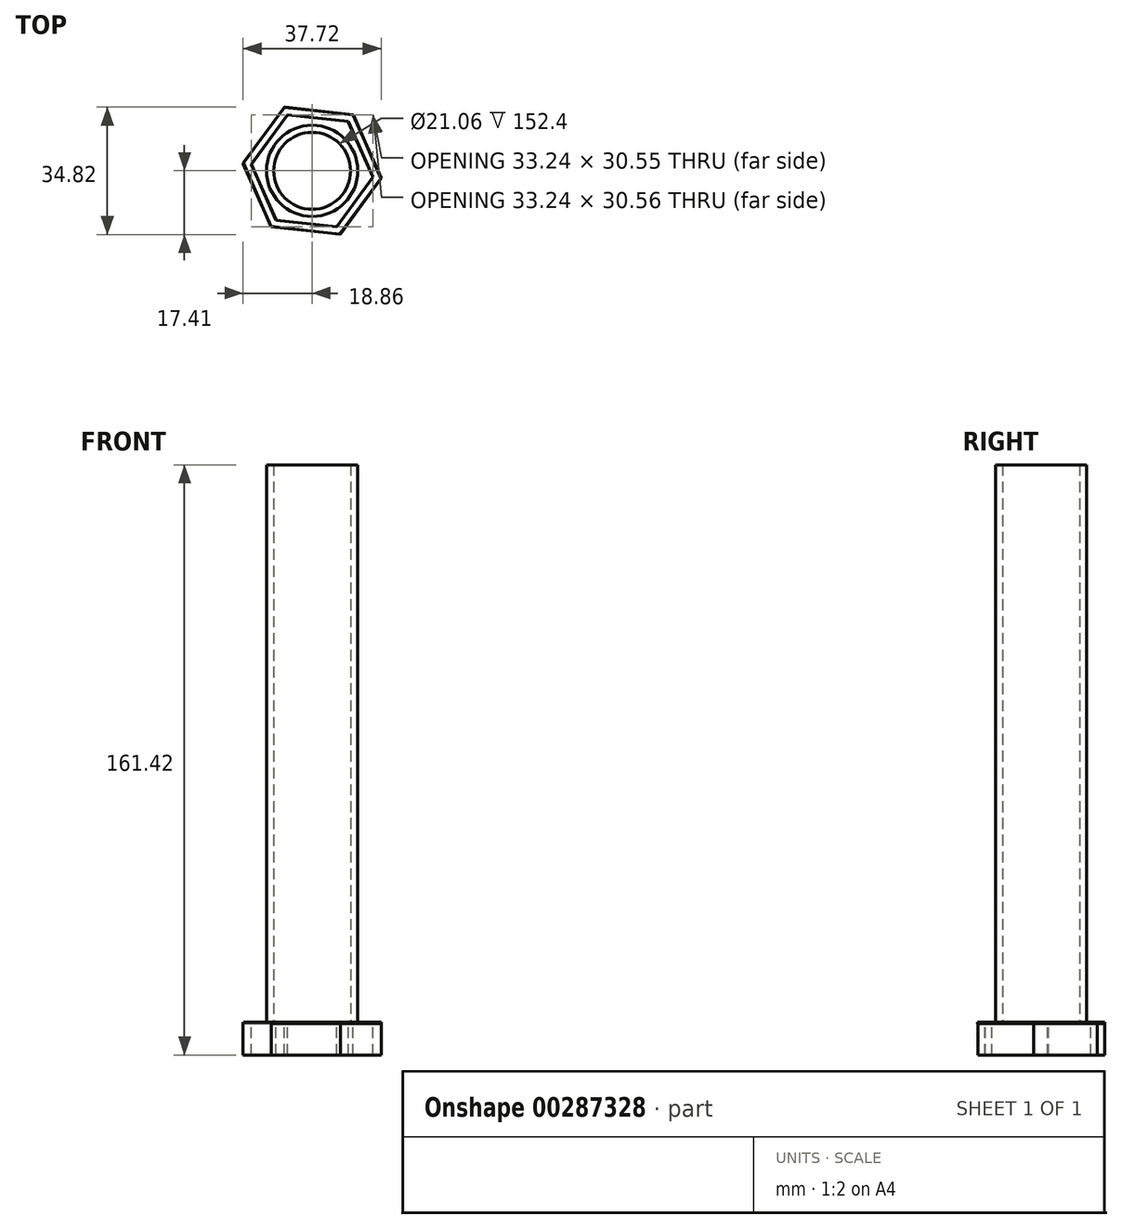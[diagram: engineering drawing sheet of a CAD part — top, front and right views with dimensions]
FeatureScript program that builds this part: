
annotation { "Feature Type Name" : "Feature", "Feature Type Description" : "" }
export const myFeature = defineFeature(function(context is Context, id is Id, definition is map)
    precondition{}
    {
        {
            var Q0;
            Q0=qCreatedBy(makeId("Top.planeOp"),FACE);
            var sketch = newSketch(context, id + "F0", { "sketchPlane" : qUnion([Q0])});
            skCircle(sketch, "E0.cCircle", {"center": v(0, 0) * mm, "radius": 14.47 * mm, "construction": true});
            skLineSegment(sketch, "E0.0", {"start": v(16.62, -1.78) * mm, "end": v(6.77, -15.28) * mm});
            skLineSegment(sketch, "E0.1", {"start": v(6.77, -15.28) * mm, "end": v(-9.85, -13.5) * mm});
            skLineSegment(sketch, "E0.2", {"start": v(-9.85, -13.5) * mm, "end": v(-16.62, 1.78) * mm});
            skLineSegment(sketch, "E0.3", {"start": v(-16.62, 1.78) * mm, "end": v(-6.77, 15.28) * mm});
            skLineSegment(sketch, "E0.4", {"start": v(-6.77, 15.28) * mm, "end": v(9.85, 13.5) * mm});
            skLineSegment(sketch, "E0.5", {"start": v(9.85, 13.5) * mm, "end": v(16.62, -1.78) * mm});
            skPoint(sketch, "E0.0.midPoint", {"position": v(11.7, -8.53) * mm});
            skCircle(sketch, "E1.cCircle", {"center": v(0, 0) * mm, "radius": 16.43 * mm, "construction": true});
            skLineSegment(sketch, "E1.0", {"start": v(18.86, -2.02) * mm, "end": v(7.69, -17.34) * mm});
            skLineSegment(sketch, "E1.1", {"start": v(7.69, -17.34) * mm, "end": v(-11.18, -15.33) * mm});
            skLineSegment(sketch, "E1.2", {"start": v(-11.18, -15.33) * mm, "end": v(-18.86, 2.02) * mm});
            skLineSegment(sketch, "E1.3", {"start": v(-18.86, 2.02) * mm, "end": v(-7.69, 17.34) * mm});
            skLineSegment(sketch, "E1.4", {"start": v(-7.69, 17.34) * mm, "end": v(11.18, 15.33) * mm});
            skLineSegment(sketch, "E1.5", {"start": v(11.18, 15.33) * mm, "end": v(18.86, -2.02) * mm});
            skPoint(sketch, "E1.0.midPoint", {"position": v(13.28, -9.68) * mm});
            skSolve(sketch);
        }
        {
            var Q0;
            Q0=makeQuery(id+"F0.imprint","IMPRINT",FACE,{"disambiguationData":[TD([[makeQuery(id+"F0.imprint","IMPRINT",EDGE,{"derivedFrom":sQuery(id+"F0.wireOp",EDGE,"E0.0")}),1.0]])]});
            extrude(context, id + "F1", {"entities" : qUnion([Q0]), "oppositeDirection" : true, "depth" : 9.02 * mm});
        }
        {
            var Q0;
            Q0=qCreatedBy(makeId("Top.planeOp"),FACE);
            var sketch = newSketch(context, id + "F2", { "sketchPlane" : qUnion([Q0])});
            skCircle(sketch, "E2", {"center": v(0, 0) * mm, "radius": 10.53 * mm});
            skCircle(sketch, "E3", {"center": v(0, 0) * mm, "radius": 12.48 * mm});
            skSolve(sketch);
        }
        {
            var Q0;
            Q0=makeQuery(id+"F2.imprint","IMPRINT",FACE,{"disambiguationData":[TD([[makeQuery(id+"F2.imprint","IMPRINT",EDGE,{"derivedFrom":sQuery(id+"F2.wireOp",EDGE,"E2")}),-1.0]])]});
            extrude(context, id + "F3", {"entities" : qUnion([Q0]), "depth" : 152.4 * mm});
        }
        {
            var Q0;
            Q0=makeQuery(id+"F0.imprint","IMPRINT",FACE,{"disambiguationData":[TD([[makeQuery(id+"F0.imprint","IMPRINT",EDGE,{"derivedFrom":sQuery(id+"F0.wireOp",EDGE,"E0.0")}),-1.0]])]});
            var sketch = newSketch(context, id + "F4", { "sketchPlane" : qUnion([Q0])});
            skCircle(sketch, "E4.cCircle", {"center": v(0, 0) * mm, "radius": 14.47 * mm, "construction": true});
            skLineSegment(sketch, "E4.0", {"start": v(16.6, -1.93) * mm, "end": v(6.63, -15.34) * mm});
            skLineSegment(sketch, "E4.1", {"start": v(6.63, -15.34) * mm, "end": v(-9.97, -13.41) * mm});
            skLineSegment(sketch, "E4.2", {"start": v(-9.97, -13.41) * mm, "end": v(-16.6, 1.93) * mm});
            skLineSegment(sketch, "E4.3", {"start": v(-16.6, 1.93) * mm, "end": v(-6.63, 15.34) * mm});
            skLineSegment(sketch, "E4.4", {"start": v(-6.63, 15.34) * mm, "end": v(9.97, 13.41) * mm});
            skLineSegment(sketch, "E4.5", {"start": v(9.97, 13.41) * mm, "end": v(16.6, -1.93) * mm});
            skPoint(sketch, "E4.0.midPoint", {"position": v(11.62, -8.63) * mm});
            skSolve(sketch);
        }
        {
            var Q0;
            Q0=qCreatedBy(makeId("Top.planeOp"),FACE);
            var sketch = newSketch(context, id + "F5", { "sketchPlane" : qUnion([Q0])});
            skCircle(sketch, "E5", {"center": v(0, 0) * mm, "radius": 10.53 * mm});
            skSolve(sketch);
        }
        {
            var Q0;
            Q0 = qSketchRegion(id + "F5", true);
            extrude(context, id + "F6", {"entities" : qUnion([Q0]), "operationType" : NewBodyOperationType.REMOVE, "depth" : 25.4 * mm});
        }
        {
            var Q0;
            Q0=qCreatedBy(makeId("Top.planeOp"),FACE);
            var sketch = newSketch(context, id + "F7", { "sketchPlane" : qUnion([Q0])});
            skCircle(sketch, "E6.cCircle", {"center": v(0, 0) * mm, "radius": 14.47 * mm, "construction": true});
            skLineSegment(sketch, "E6.0", {"start": v(16.62, -1.78) * mm, "end": v(6.77, -15.28) * mm});
            skLineSegment(sketch, "E6.1", {"start": v(6.77, -15.28) * mm, "end": v(-9.85, -13.5) * mm});
            skLineSegment(sketch, "E6.2", {"start": v(-9.85, -13.5) * mm, "end": v(-16.62, 1.78) * mm});
            skLineSegment(sketch, "E6.3", {"start": v(-16.62, 1.78) * mm, "end": v(-6.77, 15.28) * mm});
            skLineSegment(sketch, "E6.4", {"start": v(-6.77, 15.28) * mm, "end": v(9.85, 13.5) * mm});
            skLineSegment(sketch, "E6.5", {"start": v(9.85, 13.5) * mm, "end": v(16.62, -1.78) * mm});
            skPoint(sketch, "E6.0.midPoint", {"position": v(11.7, -8.53) * mm});
            skSolve(sketch);
        }
        {
            var Q0;
            Q0 = qSketchRegion(id + "F7", true);
            extrude(context, id + "F8", {"entities" : qUnion([Q0]), "oppositeDirection" : true, "depth" : 0.38 * mm});
        }
        {
            var Q0;
            Q0=qCreatedBy(makeId("Top.planeOp"),FACE);
            var sketch = newSketch(context, id + "F9", { "sketchPlane" : qUnion([Q0])});
            skCircle(sketch, "E7.cCircle", {"center": v(0, 0) * mm, "radius": 14.47 * mm, "construction": true});
            skLineSegment(sketch, "E7.0", {"start": v(16.62, -1.76) * mm, "end": v(6.78, -15.28) * mm});
            skLineSegment(sketch, "E7.1", {"start": v(6.78, -15.28) * mm, "end": v(-9.84, -13.51) * mm});
            skLineSegment(sketch, "E7.2", {"start": v(-9.84, -13.51) * mm, "end": v(-16.62, 1.76) * mm});
            skLineSegment(sketch, "E7.3", {"start": v(-16.62, 1.76) * mm, "end": v(-6.78, 15.28) * mm});
            skLineSegment(sketch, "E7.4", {"start": v(-6.78, 15.28) * mm, "end": v(9.84, 13.51) * mm});
            skLineSegment(sketch, "E7.5", {"start": v(9.84, 13.51) * mm, "end": v(16.62, -1.76) * mm});
            skPoint(sketch, "E7.0.midPoint", {"position": v(11.7, -8.52) * mm});
            skCircle(sketch, "E8.cCircle", {"center": v(0, 0) * mm, "radius": 16.43 * mm, "construction": true});
            skLineSegment(sketch, "E8.0", {"start": v(18.85, -2.16) * mm, "end": v(7.55, -17.4) * mm});
            skLineSegment(sketch, "E8.1", {"start": v(7.55, -17.4) * mm, "end": v(-11.3, -15.24) * mm});
            skLineSegment(sketch, "E8.2", {"start": v(-11.3, -15.24) * mm, "end": v(-18.85, 2.16) * mm});
            skLineSegment(sketch, "E8.3", {"start": v(-18.85, 2.16) * mm, "end": v(-7.55, 17.4) * mm});
            skLineSegment(sketch, "E8.4", {"start": v(-7.55, 17.4) * mm, "end": v(11.3, 15.24) * mm});
            skLineSegment(sketch, "E8.5", {"start": v(11.3, 15.24) * mm, "end": v(18.85, -2.16) * mm});
            skPoint(sketch, "E8.0.midPoint", {"position": v(13.2, -9.78) * mm});
            skSolve(sketch);
        }
        {
            var Q0;
            Q0 = qSketchRegion(id + "F9", true);
            extrude(context, id + "F10", {"entities" : qUnion([Q0]), "oppositeDirection" : true, "depth" : 0.38 * mm});
        }
        {
            var Q0;
            Q0=qCreatedBy(makeId("Top.planeOp"),FACE);
            var sketch = newSketch(context, id + "F11", { "sketchPlane" : qUnion([Q0])});
            skCircle(sketch, "E9", {"center": v(0, 0) * mm, "radius": 10.53 * mm});
            skSolve(sketch);
        }
        {
            var Q0;
            Q0 = qSketchRegion(id + "F11", true);
            extrude(context, id + "F12", {"entities" : qUnion([Q0]), "operationType" : NewBodyOperationType.REMOVE, "depth" : 25.4 * mm});
        }
    });
